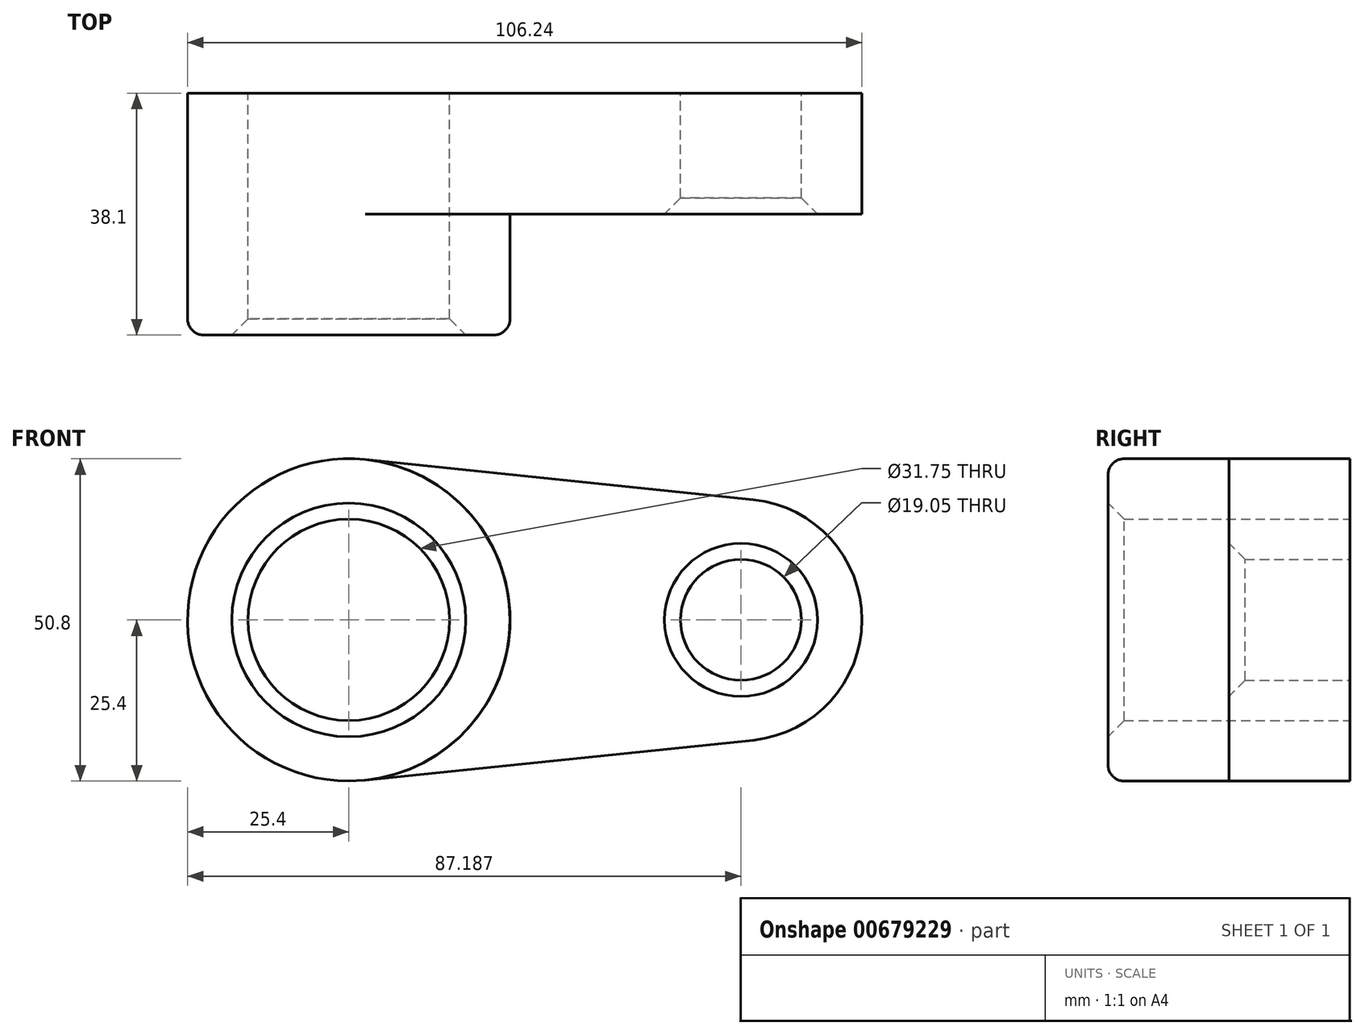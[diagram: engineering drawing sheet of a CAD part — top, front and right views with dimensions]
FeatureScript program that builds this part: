
annotation { "Feature Type Name" : "Feature", "Feature Type Description" : "" }
export const myFeature = defineFeature(function(context is Context, id is Id, definition is map)
    precondition{}
    {
        {
            var Q0;
            Q0=qCreatedBy(makeId("Front.planeOp"),FACE);
            var sketch = newSketch(context, id + "F0", { "sketchPlane" : qUnion([Q0])});
            skCircle(sketch, "E0", {"center": v(0, 0) * mm, "radius": 25.4 * mm});
            skCircle(sketch, "E1", {"center": v(61.79, 0) * mm, "radius": 19.05 * mm});
            skLineSegment(sketch, "E2", {"start": v(2.61, 25.27) * mm, "end": v(63.74, 18.95) * mm});
            skLineSegment(sketch, "E3", {"start": v(2.61, -25.27) * mm, "end": v(63.74, -18.95) * mm});
            skCircle(sketch, "E4", {"center": v(0, 0) * mm, "radius": 15.88 * mm});
            skCircle(sketch, "E5", {"center": v(61.79, 0) * mm, "radius": 9.53 * mm});
            skSolve(sketch);
        }
        {
            var Q0;
            Q0=makeQuery(id+"F0.imprint","IMPRINT",FACE,{"disambiguationData":[TD([[makeQuery(id+"F0.imprint","IMPRINT",EDGE,{"derivedFrom":sQuery(id+"F0.wireOp",EDGE,"E4")}),-1.0]])]});
            extrude(context, id + "F1", {"entities" : qUnion([Q0]), "depth" : 38.1 * mm, "offsetDistance" : 25.4 * mm});
        }
        {
            var Q0;
            Q0 = qSketchRegion(id + "F0", true);
            extrude(context, id + "F2", {"entities" : qUnion([Q0]), "operationType" : NewBodyOperationType.ADD, "depth" : 19.05 * mm, "offsetDistance" : 25.4 * mm});
        }
        {
            var Q0;
            Q0=makeQuery(id+"F1.opExtrude","CAP_EDGE",EDGE,{"disambiguationData":[OSD([sQuery(id+"F0.wireOp",EDGE,"E0")])],"isStart":false});
            fillet(context, id + "F3", {"entities" : qUnion([Q0]), "radius" : 2.54 * mm, "tangentPropagation" : true, "allowEdgeOverflow" : false});
        }
        {
            var Q0;
            Q0=makeQuery(id+"F1.opExtrude","CAP_EDGE",EDGE,{"disambiguationData":[OSD([sQuery(id+"F0.wireOp",EDGE,"E4")])],"isStart":false});
            var Q1;
            Q1=makeQuery(id+"F2.opExtrude","CAP_EDGE",EDGE,{"disambiguationData":[OSD([sQuery(id+"F0.wireOp",EDGE,"E5")])],"isStart":false});
            chamfer(context, id + "F4", {"entities" : qUnion([Q0, Q1]), "width" : 2.54 * mm, "tangentPropagation" : true});
        }
    });
